# Revit family: result
name_source: partatom
category: Generic Models
revit_build: Autodesk Revit 2015 (Build: 20140903_1530(x64)
units: mm (PartAtom-declared; Revit-internal decimal feet)

## types (1)
- Default
    Brand url = http://www.gessi.it
    Design country = Italy
    Edition number = 1
    IFC Classification = Furnishing Element
    Installation instructions = https://www.gessi.com
    Manufacturer country = Italy
    Manufacturer name = Gessi
    Material main = Brass
    Material secondary = Brass
    OmniClass Code = 23-31 25 00
    OmniClass Description = Toilet and Bath Specialties
    Product Guid = bed8f99a-d3f7-4929-86fe-a61e09cd1174
    Product SKU = 65503
    Product certification = https://www.gessi.com
    Product data url = https://bimobject.com
    Product family = VENTI20
    Product group = VENTI20 ACCESSORI
    Product name = 20VENTI - 60 cm towel rail - 65503
    Product url = https://www.gessi.com
    QR code = http://bimobject.com
    Uniclass 2015 Code = Pr_40_20_76_90
    Uniclass 2015 Name = Towel rails

## geometry (parser evidence)
native form markers: Sweep x3
no freeform markers — native parametric forms only
